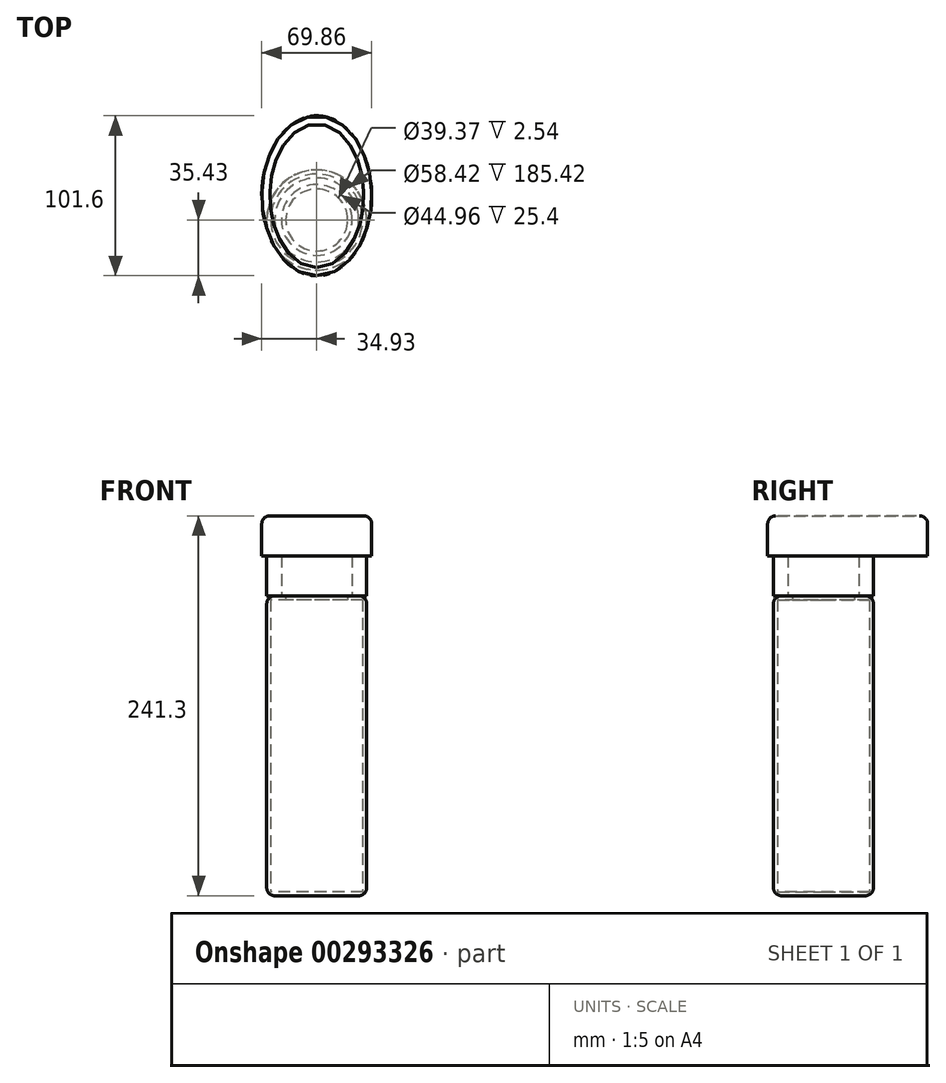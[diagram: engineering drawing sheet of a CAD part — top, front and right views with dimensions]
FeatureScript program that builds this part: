
annotation { "Feature Type Name" : "Feature", "Feature Type Description" : "" }
export const myFeature = defineFeature(function(context is Context, id is Id, definition is map)
    precondition{}
    {
        {
            var Q0;
            Q0=qCreatedBy(makeId("Top.planeOp"),FACE);
            var sketch = newSketch(context, id + "F0", { "sketchPlane" : qUnion([Q0])});
            skCircle(sketch, "E0", {"center": v(0, 0) * mm, "radius": 31.75 * mm});
            skSolve(sketch);
        }
        {
            var Q0;
            Q0 = qSketchRegion(id + "F0", true);
            extrude(context, id + "F1", {"entities" : qUnion([Q0]), "depth" : 190.5 * mm});
        }
        {
            var Q0;
            Q0=makeQuery(id+"F1.opExtrude","CAP_FACE",FACE,{"disambiguationData":[OSD([sQuery(id+"F0.wireOp",EDGE,"E0")])],"isStart":false});
            var sketch = newSketch(context, id + "F2", { "sketchPlane" : qUnion([Q0])});
            skCircle(sketch, "E1", {"center": v(0, 0) * mm, "radius": 22.23 * mm});
            skSolve(sketch);
        }
        {
            var Q0;
            Q0 = qSketchRegion(id + "F2", true);
            extrude(context, id + "F3", {"entities" : qUnion([Q0]), "operationType" : NewBodyOperationType.ADD, "depth" : 25.4 * mm});
        }
        {
            var Q0;
            Q0=makeQuery(id+"F3.opExtrude","CAP_FACE",FACE,{"disambiguationData":[OSD([sQuery(id+"F2.wireOp",EDGE,"E1")])],"isStart":false});
            shell(context, id + "F4", {"entities" : qUnion([Q0]), "thickness" : 2.54 * mm});
        }
        {
            var Q0;
            Q0=makeQuery(id+"F1.opExtrude","CAP_EDGE",EDGE,{"disambiguationData":[OSD([sQuery(id+"F0.wireOp",EDGE,"E0")])],"isStart":false});
            fillet(context, id + "F5", {"entities" : qUnion([Q0]), "radius" : 5.08 * mm, "tangentPropagation" : true, "allowEdgeOverflow" : false});
        }
        {
            var Q0;
            Q0=makeQuery(id+"F1.opExtrude","CAP_EDGE",EDGE,{"disambiguationData":[OSD([sQuery(id+"F0.wireOp",EDGE,"E0")])],"isStart":true});
            fillet(context, id + "F6", {"entities" : qUnion([Q0]), "radius" : 5.08 * mm, "tangentPropagation" : true, "allowEdgeOverflow" : false});
        }
        {
            var Q0;
            Q0=makeQuery(id+"F1.opExtrude","CAP_FACE",FACE,{"disambiguationData":[OSD([sQuery(id+"F0.wireOp",EDGE,"E0")])],"isStart":false});
            var sketch = newSketch(context, id + "F7", { "sketchPlane" : qUnion([Q0])});
            skCircle(sketch, "E2", {"center": v(0, 0) * mm, "radius": 31.75 * mm});
            skSolve(sketch);
        }
        {
            var Q0;
            Q0 = qSketchRegion(id + "F7", true);
            extrude(context, id + "F8", {"entities" : qUnion([Q0]), "depth" : 25.4 * mm});
        }
        {
            var Q0;
            Q0=makeQuery(id+"F8.opExtrude","CAP_FACE",FACE,{"disambiguationData":[OSD([sQuery(id+"F7.wireOp",EDGE,"E2")])],"isStart":false});
            var sketch = newSketch(context, id + "F9", { "sketchPlane" : qUnion([Q0])});
            skArc(sketch, "E3.0", {"start": v(-28.6, -13.77) * mm, "mid": v(0, -31.75) * mm, "end": v(28.6, -13.77) * mm});
            skEllipse(sketch, "E4", {"center": v(0, 15.37) * mm, "majorRadius": 50.8 * mm, "minorRadius": 34.93 * mm, "majorAxis": v(0, -1)});
            skFitSpline(sketch, "E5.0", {"points": [v(-1.17, -27.53) * mm, v(0, -27.57) * mm, v(1.17, -27.53) * mm, v(2.71, -27.36) * mm, v(4.65, -26.94) * mm, v(6.97, -26.1) * mm, v(9.3, -24.88) * mm, v(11.62, -23.3) * mm, v(13.9, -21.31) * mm, v(15.75, -19.33) * mm, v(17.17, -17.54) * mm, v(18.21, -16.1) * mm, v(19.21, -14.58) * mm, v(20.48, -12.44) * mm, v(21.94, -9.58) * mm, v(23.46, -5.88) * mm, v(24.74, -1.95) * mm, v(25.75, 2.18) * mm, v(26.5, 6.46) * mm, v(26.87, 10.14) * mm, v(27.03, 13.11) * mm, v(27.06, 15.37) * mm, v(27.03, 17.62) * mm, v(26.87, 20.6) * mm, v(26.5, 24.27) * mm, v(25.75, 28.56) * mm, v(24.74, 32.68) * mm, v(23.46, 36.62) * mm, v(21.94, 40.32) * mm, v(20.48, 43.18) * mm, v(19.21, 45.32) * mm, v(18.21, 46.84) * mm, v(17.17, 48.28) * mm, v(15.75, 50.06) * mm, v(13.9, 52.05) * mm, v(11.62, 54.03) * mm, v(9.3, 55.62) * mm, v(6.97, 56.83) * mm, v(4.65, 57.68) * mm, v(2.71, 58.1) * mm, v(1.17, 58.27) * mm, v(0, 58.3) * mm, v(-1.17, 58.27) * mm, v(-2.71, 58.1) * mm, v(-4.65, 57.68) * mm, v(-6.97, 56.83) * mm, v(-9.3, 55.62) * mm, v(-11.62, 54.03) * mm, v(-13.9, 52.05) * mm, v(-15.75, 50.06) * mm, v(-17.17, 48.28) * mm, v(-18.21, 46.84) * mm, v(-19.21, 45.32) * mm, v(-20.48, 43.18) * mm, v(-21.94, 40.32) * mm, v(-23.46, 36.62) * mm, v(-24.74, 32.68) * mm, v(-25.75, 28.56) * mm, v(-26.5, 24.27) * mm, v(-26.87, 20.6) * mm, v(-27.03, 17.62) * mm, v(-27.06, 15.37) * mm, v(-27.03, 13.11) * mm, v(-26.87, 10.14) * mm, v(-26.5, 6.46) * mm, v(-25.75, 2.18) * mm, v(-24.74, -1.95) * mm, v(-23.46, -5.88) * mm, v(-21.94, -9.58) * mm, v(-20.48, -12.44) * mm, v(-19.21, -14.58) * mm, v(-18.21, -16.1) * mm, v(-17.17, -17.54) * mm, v(-15.75, -19.33) * mm, v(-13.9, -21.31) * mm, v(-11.62, -23.3) * mm, v(-9.3, -24.88) * mm, v(-6.97, -26.1) * mm, v(-4.65, -26.94) * mm, v(-2.71, -27.36) * mm, v(-1.17, -27.53) * mm, v(0, -27.57) * mm, v(1.17, -27.53) * mm]});
            skArc(sketch, "E6.trimOffspring", {"start": v(27.04, 16.64) * mm, "mid": v(0, 31.75) * mm, "end": v(-27.04, 16.64) * mm});
            skSolve(sketch);
        }
        {
            var Q0;
            Q0 = qSketchRegion(id + "F9", true);
            extrude(context, id + "F10", {"entities" : qUnion([Q0]), "operationType" : NewBodyOperationType.ADD, "depth" : 25.4 * mm});
        }
        {
            var Q0;
            Q0=makeQuery(id+"F10.opExtrude","CAP_EDGE",EDGE,{"disambiguationData":[OSD([sQuery(id+"F9.wireOp",EDGE,"E4")])],"isStart":false});
            fillet(context, id + "F11", {"entities" : qUnion([Q0]), "radius" : 5.08 * mm, "tangentPropagation" : true, "allowEdgeOverflow" : false});
        }
        {
            var Q0;
            Q0=makeQuery(id+"F8.opExtrude","CAP_FACE",FACE,{"disambiguationData":[OSD([sQuery(id+"F7.wireOp",EDGE,"E2")])],"isStart":true});
            var sketch = newSketch(context, id + "F12", { "sketchPlane" : qUnion([Q0])});
            skCircle(sketch, "E7", {"center": v(0, 0) * mm, "radius": 22.48 * mm});
            skSolve(sketch);
        }
        {
            var Q0;
            Q0 = qSketchRegion(id + "F12", true);
            extrude(context, id + "F13", {"entities" : qUnion([Q0]), "operationType" : NewBodyOperationType.REMOVE, "oppositeDirection" : true, "depth" : 25.4 * mm});
        }
    });
